# Revit family: ADB Electric range cookers L800
name_source: partatom
category: Equipement spécialisé
units: mm (PartAtom-declared; Revit-internal decimal feet)

## family parameters
Basée sur le plan de construction = Non
Conserver l'orientation des annotations = Non
Cote de connecteur circulaire = Utiliser le diamètre
Couper avec des vides une fois chargée = Non
Numéro OmniClass = 23.40.40.14.17.11
Partagée = Non
Repère de localisation dans la pièce = Non
Titre OmniClass = Cookers, Ovens, Stoves
Toujours verticalement = Oui
Type d'élément = Normal

## types (2) — shared parameters
B = 230 mm
C = 405 mm
Commentaires du type = Ambassade range - Electric range cookers
Fabricant = Société Industrielle de Lacanche
URL = https://www.ambassade-de-bourgogne.com
zero-valued in all types: Elévation par défaut

## per-type parameters (varying)
| type | CE 841 E | CE 841 VTR | Description | Modèle | Pbase | Table | Weight |
| 4 Electric hotplates, 1 oven 620x400 - CE 841 E | Oui | Non | Electric range cooker 4 Electric hotplates, 1 oven 620x400 - CE 841 E | CE 841 E | 11700 W | CE841E _4 plaques électriques | 98.00 kg |
| 4 Radiant rings,1  oven 620x400 - CE 841 VTR | Non | Oui | Electric range cooker 4 Radiant rings,1  oven 620x400 - CE 841 VTR | CE 841 VTR | 12500 W | CE841 VTR_4 foyers radiants | 90.00 kg |
